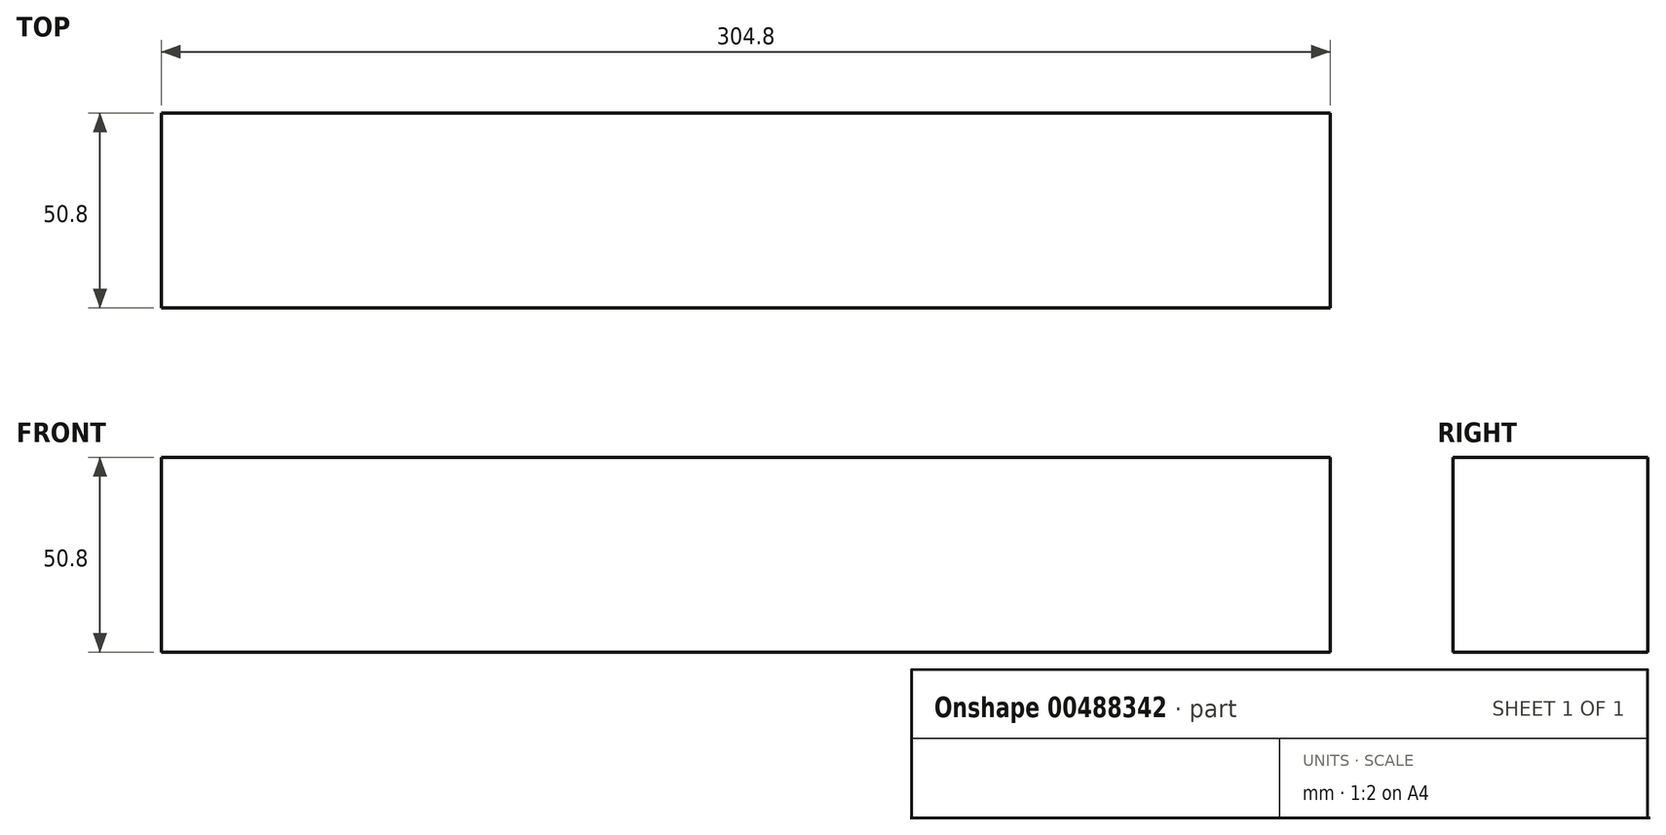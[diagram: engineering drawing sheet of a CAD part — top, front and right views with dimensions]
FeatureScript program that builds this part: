
annotation { "Feature Type Name" : "Feature", "Feature Type Description" : "" }
export const myFeature = defineFeature(function(context is Context, id is Id, definition is map)
    precondition{}
    {
        {
            var Q0;
            Q0=qCreatedBy(makeId("Right.planeOp"),FACE);
            var sketch = newSketch(context, id + "F0", { "sketchPlane" : qUnion([Q0])});
            skLineSegment(sketch, "E0.bottom", {"start": v(25.4, 25.4) * mm, "end": v(-25.4, 25.4) * mm});
            skLineSegment(sketch, "E0.top", {"start": v(25.4, -25.4) * mm, "end": v(-25.4, -25.4) * mm});
            skLineSegment(sketch, "E0.left", {"start": v(25.4, 25.4) * mm, "end": v(25.4, -25.4) * mm});
            skLineSegment(sketch, "E0.right", {"start": v(-25.4, 25.4) * mm, "end": v(-25.4, -25.4) * mm});
            skPoint(sketch, "E0.middle", {"position": v(0, 0) * mm});
            skSolve(sketch);
        }
        {
            var Q0;
            Q0 = qSketchRegion(id + "F0", true);
            extrude(context, id + "F1", {"entities" : qUnion([Q0]), "depth" : 304.8 * mm});
        }
    });
